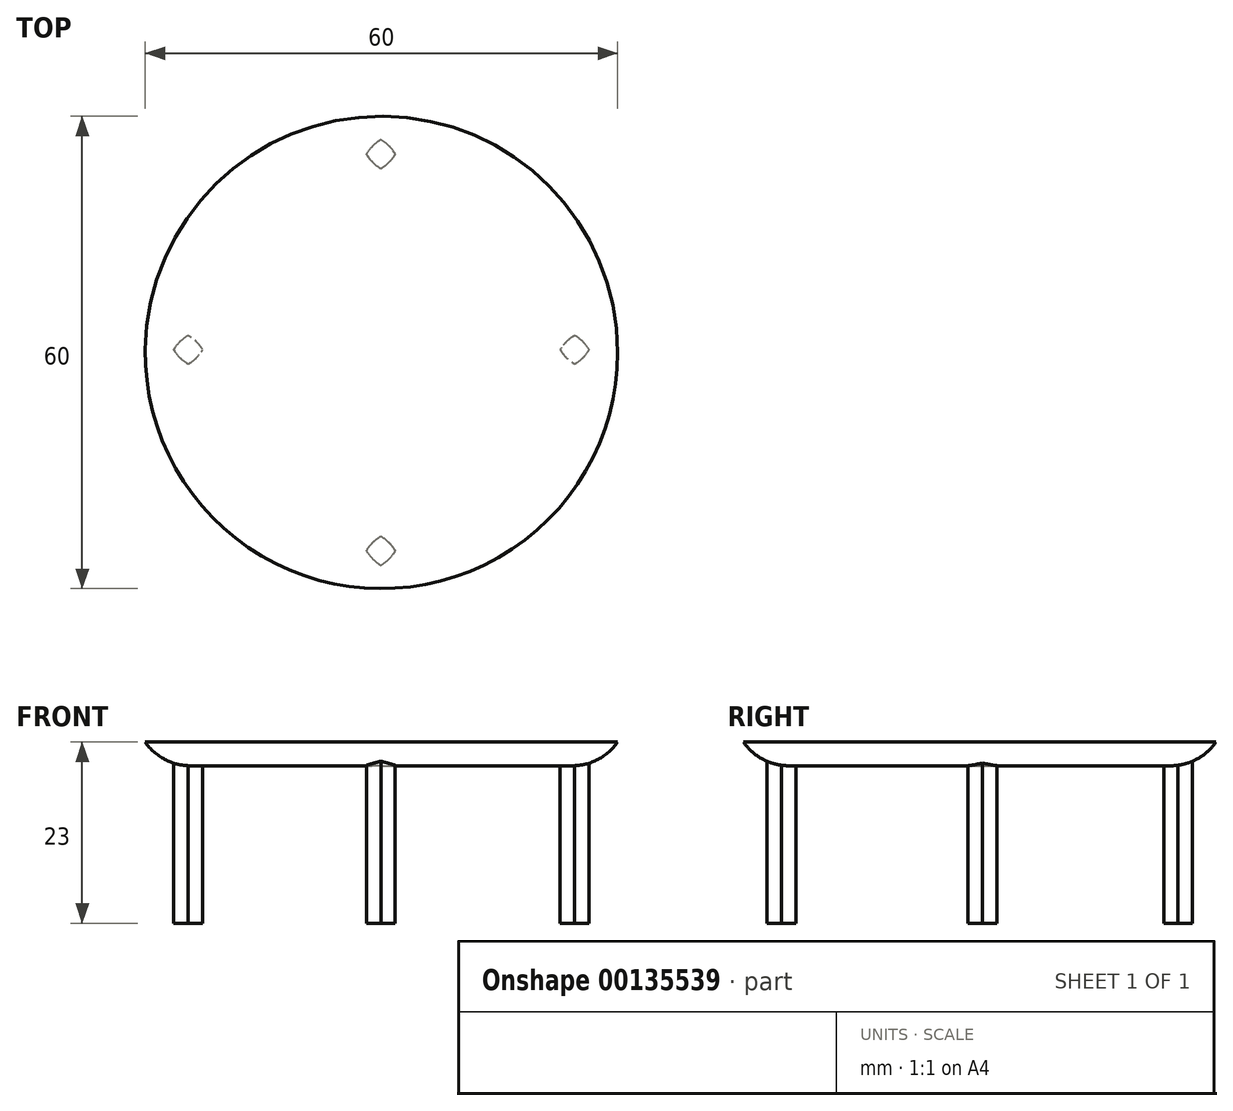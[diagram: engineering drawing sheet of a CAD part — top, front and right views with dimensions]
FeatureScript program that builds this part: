
annotation { "Feature Type Name" : "Feature", "Feature Type Description" : "" }
export const myFeature = defineFeature(function(context is Context, id is Id, definition is map)
    precondition{}
    {
        {
            var Q0;
            Q0=qCreatedBy(makeId("Top.planeOp"),FACE);
            var sketch = newSketch(context, id + "F0", { "sketchPlane" : qUnion([Q0])});
            skCircle(sketch, "E0", {"center": v(0, 0) * mm, "radius": 30 * mm});
            skSolve(sketch);
        }
        {
            var Q0;
            Q0 = qSketchRegion(id + "F0", true);
            extrude(context, id + "F1", {"entities" : qUnion([Q0]), "depth" : 3 * mm});
        }
        {
            var Q0;
            Q0=qCreatedBy(makeId("Top.planeOp"),FACE);
            var sketch = newSketch(context, id + "F2", { "sketchPlane" : qUnion([Q0])});
            skLineSegment(sketch, "E1.bottom", {"start": v(-27.05, 2.85) * mm, "end": v(-22.05, 2.85) * mm});
            skLineSegment(sketch, "E1.top", {"start": v(-27.05, -2.15) * mm, "end": v(-22.05, -2.15) * mm});
            skLineSegment(sketch, "E1.left", {"start": v(-27.05, 2.85) * mm, "end": v(-27.05, -2.15) * mm});
            skLineSegment(sketch, "E1.right", {"start": v(-22.05, 2.85) * mm, "end": v(-22.05, -2.15) * mm});
            skLineSegment(sketch, "E2.MirrorCS", {"start": v(27.05, 2.85) * mm, "end": v(22.05, 2.85) * mm});
            skLineSegment(sketch, "E3.MirrorCS", {"start": v(27.05, 2.85) * mm, "end": v(27.05, -2.15) * mm});
            skLineSegment(sketch, "E4.MirrorCS", {"start": v(27.05, -2.15) * mm, "end": v(22.05, -2.15) * mm});
            skLineSegment(sketch, "E5.MirrorCS", {"start": v(22.05, 2.85) * mm, "end": v(22.05, -2.15) * mm});
            skSolve(sketch);
        }
        {
            var Q0;
            Q0 = qSketchRegion(id + "F2", true);
            extrude(context, id + "F3", {"entities" : qUnion([Q0]), "operationType" : NewBodyOperationType.ADD, "oppositeDirection" : true, "depth" : 20 * mm});
        }
        {
            var Q0;
            Q0=qCreatedBy(makeId("Top.planeOp"),FACE);
            var sketch = newSketch(context, id + "F4", { "sketchPlane" : qUnion([Q0])});
            skLineSegment(sketch, "E6.bottom", {"start": v(-2.57, 27.7) * mm, "end": v(2.43, 27.7) * mm});
            skLineSegment(sketch, "E6.top", {"start": v(-2.57, 22.7) * mm, "end": v(2.43, 22.7) * mm});
            skLineSegment(sketch, "E6.left", {"start": v(-2.57, 27.7) * mm, "end": v(-2.57, 22.7) * mm});
            skLineSegment(sketch, "E6.right", {"start": v(2.43, 27.7) * mm, "end": v(2.43, 22.7) * mm});
            skLineSegment(sketch, "E7.MirrorCS", {"start": v(-2.57, -22.7) * mm, "end": v(2.43, -22.7) * mm});
            skLineSegment(sketch, "E8.MirrorCS", {"start": v(-2.57, -27.7) * mm, "end": v(-2.57, -22.7) * mm});
            skLineSegment(sketch, "E9.MirrorCS", {"start": v(-2.57, -27.7) * mm, "end": v(2.43, -27.7) * mm});
            skLineSegment(sketch, "E10.MirrorCS", {"start": v(2.43, -27.7) * mm, "end": v(2.43, -22.7) * mm});
            skSolve(sketch);
        }
        {
            var Q0;
            Q0 = qSketchRegion(id + "F4", true);
            extrude(context, id + "F5", {"entities" : qUnion([Q0]), "operationType" : NewBodyOperationType.ADD, "oppositeDirection" : true, "depth" : 20 * mm});
        }
        {
            var Q0;
            Q0=makeQuery(id+"F5.opExtrude","SWEPT_EDGE",EDGE,{"disambiguationData":[OSD([sQuery(id+"F4.wireOp",EDGE,"E8.MirrorCS"),sQuery(id+"F4.wireOp",EDGE,"E9.MirrorCS")])]});
            var Q1;
            Q1=makeQuery(id+"F5.opExtrude","SWEPT_EDGE",EDGE,{"disambiguationData":[OSD([sQuery(id+"F4.wireOp",EDGE,"E7.MirrorCS"),sQuery(id+"F4.wireOp",EDGE,"E8.MirrorCS")])]});
            var Q2;
            Q2=makeQuery(id+"F5.opExtrude","SWEPT_EDGE",EDGE,{"disambiguationData":[OSD([sQuery(id+"F4.wireOp",EDGE,"E7.MirrorCS"),sQuery(id+"F4.wireOp",EDGE,"E10.MirrorCS")])]});
            var Q3;
            Q3=makeQuery(id+"F5.opExtrude","SWEPT_EDGE",EDGE,{"disambiguationData":[OSD([sQuery(id+"F4.wireOp",EDGE,"E9.MirrorCS"),sQuery(id+"F4.wireOp",EDGE,"E10.MirrorCS")])]});
            var Q4;
            Q4=makeQuery(id+"F3.opExtrude","SWEPT_EDGE",EDGE,{"disambiguationData":[OSD([sQuery(id+"F2.wireOp",EDGE,"E1.bottom"),sQuery(id+"F2.wireOp",EDGE,"E1.left")])]});
            var Q5;
            Q5=makeQuery(id+"F3.opExtrude","SWEPT_EDGE",EDGE,{"disambiguationData":[OSD([sQuery(id+"F2.wireOp",EDGE,"E1.top"),sQuery(id+"F2.wireOp",EDGE,"E1.left")])]});
            var Q6;
            Q6=makeQuery(id+"F3.opExtrude","SWEPT_EDGE",EDGE,{"disambiguationData":[OSD([sQuery(id+"F2.wireOp",EDGE,"E1.top"),sQuery(id+"F2.wireOp",EDGE,"E1.right")])]});
            var Q7;
            Q7=makeQuery(id+"F3.opExtrude","SWEPT_EDGE",EDGE,{"disambiguationData":[OSD([sQuery(id+"F2.wireOp",EDGE,"E1.bottom"),sQuery(id+"F2.wireOp",EDGE,"E1.right")])]});
            var Q8;
            Q8=makeQuery(id+"F5.opExtrude","SWEPT_EDGE",EDGE,{"disambiguationData":[OSD([sQuery(id+"F4.wireOp",EDGE,"E6.bottom"),sQuery(id+"F4.wireOp",EDGE,"E6.right")])]});
            var Q9;
            Q9=makeQuery(id+"F5.opExtrude","SWEPT_EDGE",EDGE,{"disambiguationData":[OSD([sQuery(id+"F4.wireOp",EDGE,"E6.bottom"),sQuery(id+"F4.wireOp",EDGE,"E6.left")])]});
            var Q10;
            Q10=makeQuery(id+"F5.opExtrude","SWEPT_EDGE",EDGE,{"disambiguationData":[OSD([sQuery(id+"F4.wireOp",EDGE,"E6.top"),sQuery(id+"F4.wireOp",EDGE,"E6.left")])]});
            var Q11;
            Q11=makeQuery(id+"F5.opExtrude","SWEPT_EDGE",EDGE,{"disambiguationData":[OSD([sQuery(id+"F4.wireOp",EDGE,"E6.top"),sQuery(id+"F4.wireOp",EDGE,"E6.right")])]});
            var Q12;
            Q12=makeQuery(id+"F3.opExtrude","SWEPT_EDGE",EDGE,{"disambiguationData":[OSD([sQuery(id+"F2.wireOp",EDGE,"E2.MirrorCS"),sQuery(id+"F2.wireOp",EDGE,"E3.MirrorCS")])]});
            var Q13;
            Q13=makeQuery(id+"F3.opExtrude","SWEPT_EDGE",EDGE,{"disambiguationData":[OSD([sQuery(id+"F2.wireOp",EDGE,"E4.MirrorCS"),sQuery(id+"F2.wireOp",EDGE,"E3.MirrorCS")])]});
            var Q14;
            Q14=makeQuery(id+"F3.opExtrude","SWEPT_EDGE",EDGE,{"disambiguationData":[OSD([sQuery(id+"F2.wireOp",EDGE,"E2.MirrorCS"),sQuery(id+"F2.wireOp",EDGE,"E5.MirrorCS")])]});
            var Q15;
            Q15=makeQuery(id+"F3.opExtrude","SWEPT_EDGE",EDGE,{"disambiguationData":[OSD([sQuery(id+"F2.wireOp",EDGE,"E4.MirrorCS"),sQuery(id+"F2.wireOp",EDGE,"E5.MirrorCS")])]});
            fillet(context, id + "F6", {"entities" : qUnion([Q0, Q1, Q2, Q3, Q4, Q5, Q6, Q7, Q8, Q9, Q10, Q11, Q12, Q13, Q14, Q15]), "radius" : 5 * mm, "tangentPropagation" : true, "allowEdgeOverflow" : false});
        }
        {
            var Q0;
            Q0=makeQuery(id+"F1.opExtrude","CAP_EDGE",EDGE,{"disambiguationData":[OSD([sQuery(id+"F0.wireOp",EDGE,"E0")])],"isStart":true});
            fillet(context, id + "F7", {"entities" : qUnion([Q0]), "radius" : 7 * mm, "tangentPropagation" : true, "allowEdgeOverflow" : false});
        }
    });
